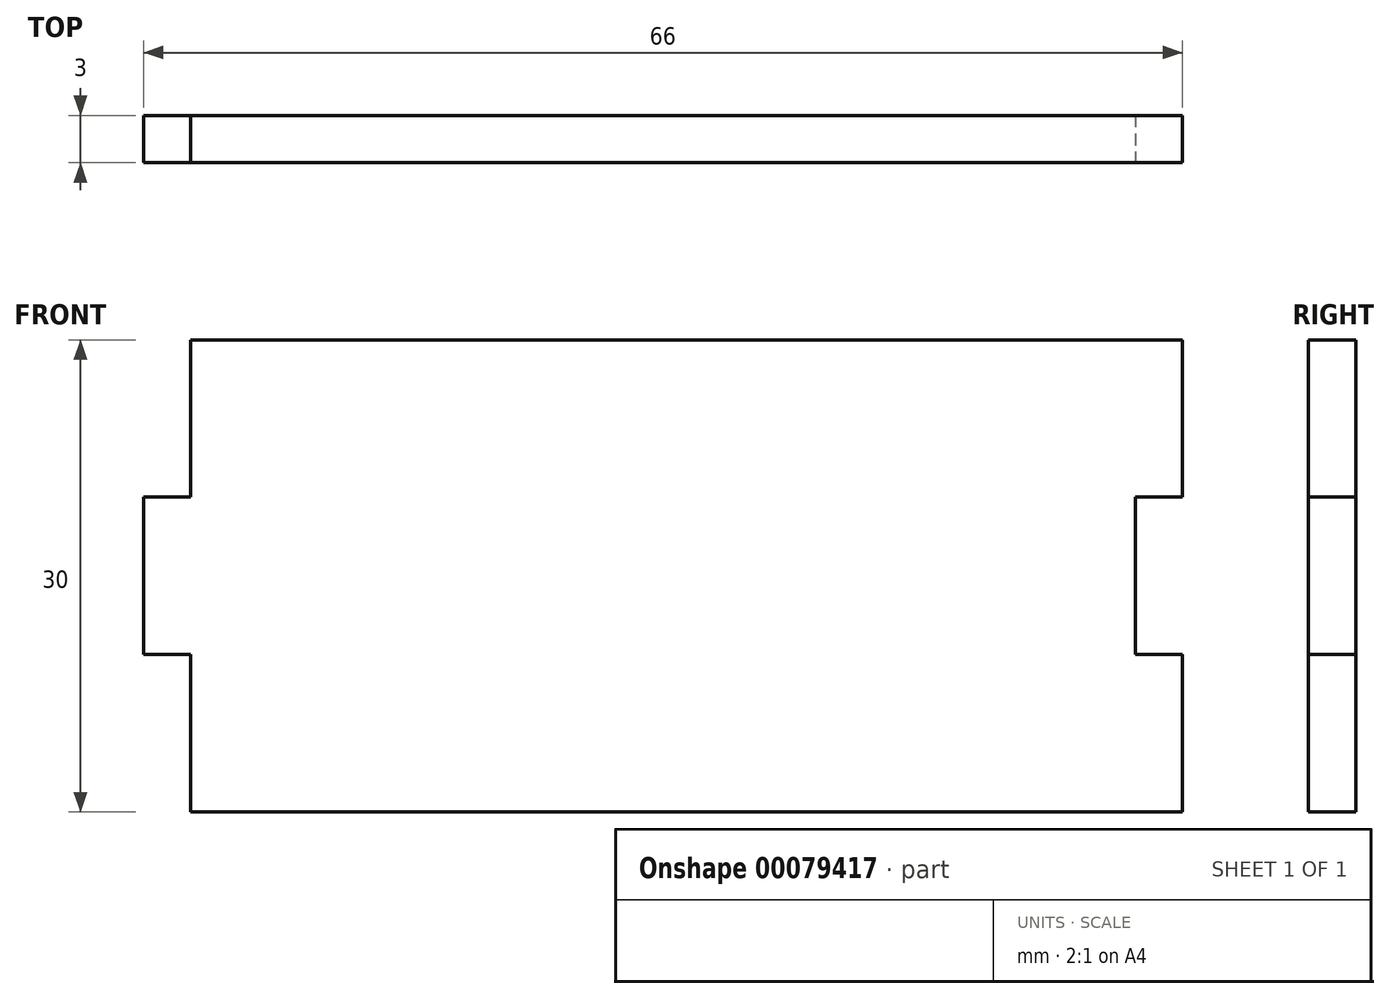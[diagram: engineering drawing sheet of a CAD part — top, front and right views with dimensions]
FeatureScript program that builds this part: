
annotation { "Feature Type Name" : "Feature", "Feature Type Description" : "" }
export const myFeature = defineFeature(function(context is Context, id is Id, definition is map)
    precondition{}
    {
        {
            var Q0;
            Q0=qCreatedBy(makeId("Top.planeOp"),FACE);
            var sketch = newSketch(context, id + "F0", { "sketchPlane" : qUnion([Q0])});
            skLineSegment(sketch, "E0.bottom", {"start": v(-28.26, 0.98) * mm, "end": v(31.74, 0.98) * mm});
            skLineSegment(sketch, "E0.top", {"start": v(-28.26, -2.02) * mm, "end": v(31.74, -2.02) * mm});
            skLineSegment(sketch, "E0.left", {"start": v(-28.26, 0.98) * mm, "end": v(-28.26, -2.02) * mm});
            skLineSegment(sketch, "E0.right", {"start": v(31.74, 0.98) * mm, "end": v(31.74, -2.02) * mm});
            skSolve(sketch);
        }
        {
            var Q0;
            Q0=makeQuery(id+"F0.imprint","IMPRINT",FACE,{"disambiguationData":[TD([[makeQuery(id+"F0.imprint","IMPRINT",EDGE,{"derivedFrom":sQuery(id+"F0.wireOp",EDGE,"E0.bottom")}),-1.0]])]});
            extrude(context, id + "F1", {"entities" : qUnion([Q0]), "depth" : 30 * mm});
        }
        {
            var Q0;
            Q0=makeQuery(id+"F1.opExtrude","SWEPT_FACE",FACE,{"disambiguationData":[OSD([sQuery(id+"F0.wireOp",EDGE,"E0.right")])]});
            var sketch = newSketch(context, id + "F2", { "sketchPlane" : qUnion([Q0])});
            skLineSegment(sketch, "E1.bottom", {"start": v(-2.02, 30) * mm, "end": v(0.98, 30) * mm});
            skLineSegment(sketch, "E1.top", {"start": v(-2.02, 20) * mm, "end": v(0.98, 20) * mm});
            skLineSegment(sketch, "E1.left", {"start": v(-2.02, 30) * mm, "end": v(-2.02, 20) * mm});
            skLineSegment(sketch, "E1.right", {"start": v(0.98, 30) * mm, "end": v(0.98, 20) * mm});
            skLineSegment(sketch, "E2.bottom", {"start": v(0.98, 0) * mm, "end": v(-2.02, 0) * mm});
            skLineSegment(sketch, "E2.top", {"start": v(0.98, 10) * mm, "end": v(-2.02, 10) * mm});
            skLineSegment(sketch, "E2.left", {"start": v(0.98, 0) * mm, "end": v(0.98, 10) * mm});
            skLineSegment(sketch, "E2.right", {"start": v(-2.02, 0) * mm, "end": v(-2.02, 10) * mm});
            skSolve(sketch);
        }
        {
            var Q0;
            Q0=makeQuery(id+"F2.imprint","IMPRINT",FACE,{"disambiguationData":[TD([[makeQuery(id+"F2.imprint","IMPRINT",EDGE,{"derivedFrom":sQuery(id+"F2.wireOp",EDGE,"E1.bottom")}),1.0]])]});
            var Q1;
            Q1=makeQuery(id+"F2.imprint","IMPRINT",FACE,{"disambiguationData":[TD([[makeQuery(id+"F2.imprint","IMPRINT",EDGE,{"derivedFrom":sQuery(id+"F2.wireOp",EDGE,"E2.bottom")}),-1.0]])]});
            extrude(context, id + "F3", {"entities" : qUnion([Q0, Q1]), "operationType" : NewBodyOperationType.ADD, "depth" : 3 * mm});
        }
        {
            var Q0;
            Q0=makeQuery(id+"F1.opExtrude","SWEPT_FACE",FACE,{"disambiguationData":[OSD([sQuery(id+"F0.wireOp",EDGE,"E0.left")])]});
            var sketch = newSketch(context, id + "F4", { "sketchPlane" : qUnion([Q0])});
            skLineSegment(sketch, "E3.bottom", {"start": v(-0.98, 30) * mm, "end": v(2.02, 30) * mm});
            skLineSegment(sketch, "E3.top", {"start": v(-0.98, 20) * mm, "end": v(2.02, 20) * mm});
            skLineSegment(sketch, "E3.left", {"start": v(-0.98, 30) * mm, "end": v(-0.98, 20) * mm});
            skLineSegment(sketch, "E3.right", {"start": v(2.02, 30) * mm, "end": v(2.02, 20) * mm});
            skLineSegment(sketch, "E4.top", {"start": v(-0.98, 10) * mm, "end": v(2.02, 10) * mm});
            skLineSegment(sketch, "E4.left", {"start": v(-0.98, 20) * mm, "end": v(-0.98, 10) * mm});
            skLineSegment(sketch, "E4.right", {"start": v(2.02, 20) * mm, "end": v(2.02, 10) * mm});
            skSolve(sketch);
        }
        {
            var Q0;
            Q0=makeQuery(id+"F4.imprint","IMPRINT",FACE,{"disambiguationData":[TD([[makeQuery(id+"F4.imprint","IMPRINT",EDGE,{"derivedFrom":sQuery(id+"F4.wireOp",EDGE,"E3.top")}),-1.0]])]});
            extrude(context, id + "F5", {"entities" : qUnion([Q0]), "operationType" : NewBodyOperationType.ADD, "depth" : 3 * mm});
        }
    });
